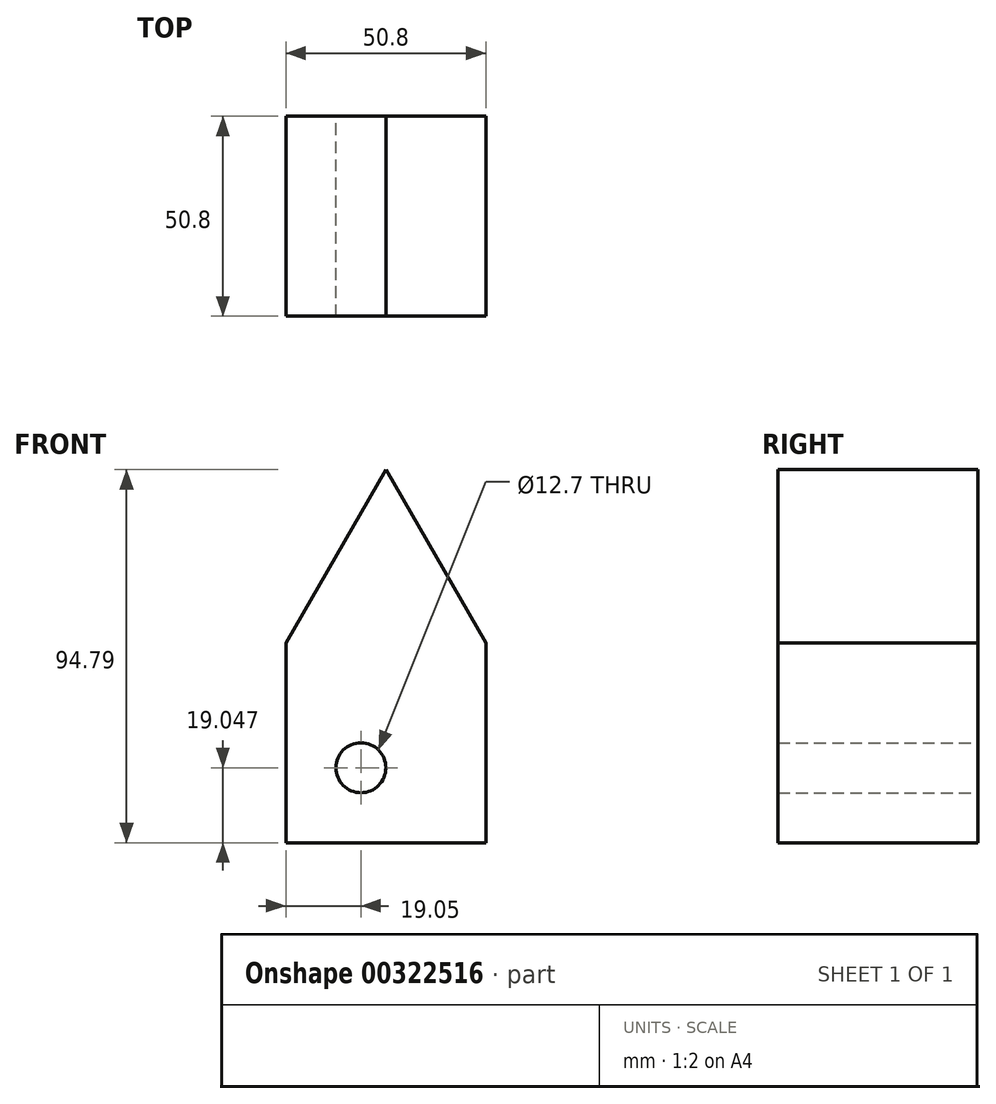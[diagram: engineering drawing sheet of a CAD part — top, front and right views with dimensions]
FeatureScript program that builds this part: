
annotation { "Feature Type Name" : "Feature", "Feature Type Description" : "" }
export const myFeature = defineFeature(function(context is Context, id is Id, definition is map)
    precondition{}
    {
        {
            var Q0;
            Q0=qCreatedBy(makeId("Front.planeOp"),FACE);
            var sketch = newSketch(context, id + "F0", { "sketchPlane" : qUnion([Q0])});
            skLineSegment(sketch, "E0.top", {"start": v(-25.4, -56.25) * mm, "end": v(25.4, -56.25) * mm});
            skLineSegment(sketch, "E0.left", {"start": v(-25.4, -5.45) * mm, "end": v(-25.4, -56.25) * mm});
            skLineSegment(sketch, "E0.right", {"start": v(25.4, -5.45) * mm, "end": v(25.4, -56.25) * mm});
            skLineSegment(sketch, "E1", {"start": v(-25.4, -5.45) * mm, "end": v(0, 38.54) * mm});
            skLineSegment(sketch, "E2", {"start": v(0, 38.54) * mm, "end": v(25.4, -5.45) * mm});
            skCircle(sketch, "E3", {"center": v(-6.35, -37.2) * mm, "radius": 6.35 * mm});
            skSolve(sketch);
        }
        {
            var Q0;
            Q0=makeQuery(id+"F0.imprint","IMPRINT",FACE,{"disambiguationData":[TD([[makeQuery(id+"F0.imprint","IMPRINT",EDGE,{"derivedFrom":sQuery(id+"F0.wireOp",EDGE,"E0.top")}),1.0]])]});
            extrude(context, id + "F1", {"entities" : qUnion([Q0]), "depth" : 50.8 * mm});
        }
    });
